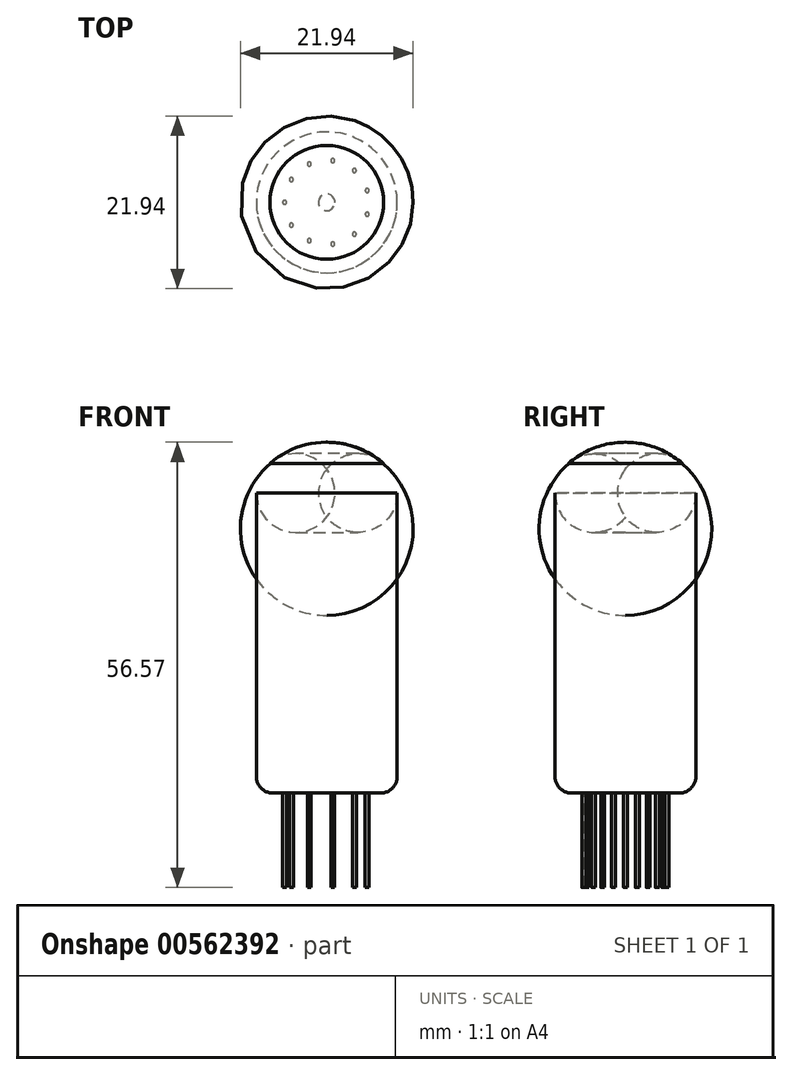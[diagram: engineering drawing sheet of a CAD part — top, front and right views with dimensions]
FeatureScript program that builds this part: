
annotation { "Feature Type Name" : "Feature", "Feature Type Description" : "" }
export const myFeature = defineFeature(function(context is Context, id is Id, definition is map)
    precondition{}
    {
        {
            var Q0;
            Q0=qCreatedBy(makeId("Right.planeOp"),FACE);
            var sketch = newSketch(context, id + "F0", { "sketchPlane" : qUnion([Q0])});
            skLineSegment(sketch, "E0", {"start": v(-8.95, 0) * mm, "end": v(-8.95, 38.1) * mm});
            skLineSegment(sketch, "E1", {"start": v(-8.95, 0) * mm, "end": v(0, 0) * mm});
            skArc(sketch, "E2", {"start": v(0, 44.57) * mm, "mid": v(-3.85, 43.88) * mm, "end": v(-7.22, 41.9) * mm});
            skPoint(sketch, "E3.visualSharp", {"position": v(-8.95, 40) * mm});
            skArc(sketch, "E3.filletArc", {"start": v(-7.22, 41.9) * mm, "mid": v(-8.5, 40.19) * mm, "end": v(-8.95, 38.1) * mm});
            skLineSegment(sketch, "E4", {"start": v(0, 0) * mm, "end": v(0, 44.57) * mm});
            skSolve(sketch);
        }
        {
            var Q0;
            Q0 = qSketchRegion(id + "F0", true);
            var Q1;
            Q1=sQuery(id+"F0.wireOp",EDGE,"E4");
            revolve(context, id + "F1", {"entities" : qUnion([Q0]), "axis" : qUnion([Q1]), "revolveType" : RevolveType.FULL});
        }
        {
            var Q0;
            Q0=makeQuery(id+"F1.opRevolve","SWEPT_EDGE",EDGE,{"disambiguationData":[OSD([sQuery(id+"F0.wireOp",EDGE,"E0"),sQuery(id+"F0.wireOp",EDGE,"E1")])]});
            fillet(context, id + "F2", {"entities" : qUnion([Q0]), "radius" : 2.1 * mm, "tangentPropagation" : true, "allowEdgeOverflow" : false});
        }
        {
            var Q0;
            Q0=makeQuery(id+"F1.opRevolve","SWEPT_FACE",FACE,{"disambiguationData":[OSD([sQuery(id+"F0.wireOp",EDGE,"E1")])]});
            var sketch = newSketch(context, id + "F3", { "sketchPlane" : qUnion([Q0])});
            skCircle(sketch, "E5", {"center": v(-5.35, 0) * mm, "radius": 0.25 * mm});
            skCircle(sketch, "E6.1.0", {"center": v(-4.5, -2.9) * mm, "radius": 0.25 * mm});
            skCircle(sketch, "E6.2.0", {"center": v(-2.22, -4.87) * mm, "radius": 0.25 * mm});
            skCircle(sketch, "E6.3.0", {"center": v(0.76, -5.3) * mm, "radius": 0.25 * mm});
            skCircle(sketch, "E6.4.0", {"center": v(3.5, -4.04) * mm, "radius": 0.25 * mm});
            skCircle(sketch, "E6.5.0", {"center": v(5.13, -1.5) * mm, "radius": 0.25 * mm});
            skCircle(sketch, "E6.6.0", {"center": v(5.13, 1.5) * mm, "radius": 0.25 * mm});
            skCircle(sketch, "E6.7.0", {"center": v(3.5, 4.04) * mm, "radius": 0.25 * mm});
            skCircle(sketch, "E6.8.0", {"center": v(0.76, 5.3) * mm, "radius": 0.25 * mm});
            skCircle(sketch, "E6.9.0", {"center": v(-2.22, 4.87) * mm, "radius": 0.25 * mm});
            skCircle(sketch, "E6.10.0", {"center": v(-4.5, 2.9) * mm, "radius": 0.25 * mm});
            skPoint(sketch, "E6.center", {"position": v(0, 0) * mm});
            skSolve(sketch);
        }
        {
            var Q0;
            Q0 = qSketchRegion(id + "F3", true);
            extrude(context, id + "F4", {"entities" : qUnion([Q0]), "operationType" : NewBodyOperationType.ADD, "depth" : 12 * mm, "offsetDistance" : 25 * mm});
        }
    });
